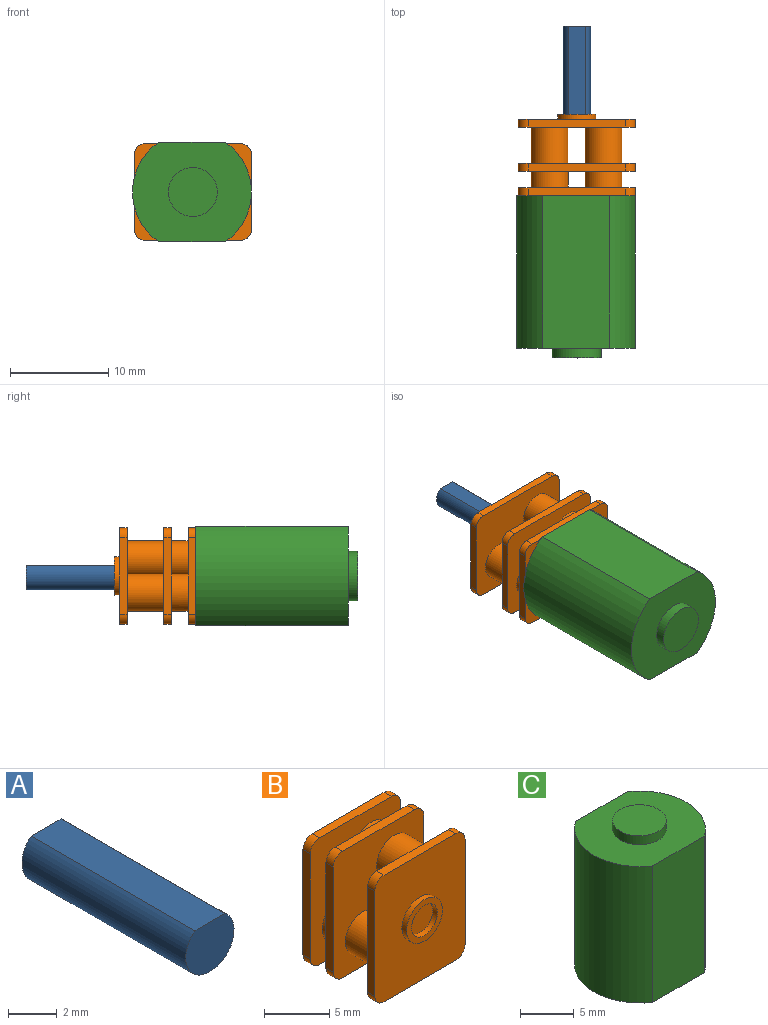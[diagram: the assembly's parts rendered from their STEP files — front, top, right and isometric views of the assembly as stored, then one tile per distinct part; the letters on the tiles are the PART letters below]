
ASSEMBLY  parts=3 mates=3
PART A: 4 faces, bbox 2.8x9.5x2.5 mm
  f0: cylinder r=1.4mm len=9.5mm, axis (0,1,0), area 65.8mm2, adj f1,f2,f3
  f1: plane 9.5x1.73mm, normal (0,0,1), area 16.5mm2, adj f0,f2,f3
  f2: plane 2.8x2.5mm, normal (0,-1,0), area 5.8mm2, adj f0,f1
  f3: plane 2.8x2.5mm, normal (0,1,0), area 5.8mm2, adj f0,f1
PART B: 38 faces, bbox 9.8x8.3x11.9 mm
  f0: plane 9.9x0.8mm, normal (1,0,0), area 7.9mm2, adj f19,f20,f26,f30
  f1: plane 9.9x0.8mm, normal (1,0,0), area 7.9mm2, adj f16,f17,f25,f28
  f2: plane 9.9x0.8mm, normal (-1,0,0), area 7.9mm2, adj f19,f20,f27,f33
  f3: plane 9.9x0.8mm, normal (-1,0,0), area 7.9mm2, adj f16,f17,f23,f29
  f4: plane 7.8x0.8mm, normal (0,0,-1), area 6.2mm2, adj f19,f20,f30,f33
  f5: plane 7.8x0.8mm, normal (0,0,-1), area 6.2mm2, adj f16,f17,f23,f25
  f6: plane 7.8x0.8mm, normal (0,0,-1), area 6.2mm2, adj f11,f15,f22,f24
  f7: cylinder r=1.9mm len=3.8mm, axis (0,1,0), area 44.2mm2, adj f16,f19
  f8: cylinder r=1.9mm len=3.8mm, axis (0,1,0), area 44.2mm2, adj f16,f19
  f9: cylinder r=1.9mm len=3.8mm, axis (0,1,0), area 20.3mm2, adj f11,f17
  f10: cylinder r=1.9mm len=3.8mm, axis (0,1,0), area 20.3mm2, adj f11,f17
  f11: plane 11.9x9.8mm, normal (0,-1,0), area 93.1mm2, adj f6,f9,f10,f12,f13,f14,f22,f24
  f12: plane 9.9x0.8mm, normal (1,0,0), area 7.9mm2, adj f11,f15,f24,f31
  f13: plane 7.8x0.8mm, normal (0,0,1), area 6.2mm2, adj f11,f15,f31,f32
  f14: plane 9.9x0.8mm, normal (-1,0,0), area 7.9mm2, adj f11,f15,f22,f32
  f15: plane 11.9x9.8mm, normal (0,1,0), area 115.8mm2, adj f6,f12,f13,f14,f22,f24,f31,f32
  f16: plane 11.9x9.8mm, normal (0,-1,0), area 93.1mm2, adj f1,f3,f5,f7,f8,f18,f23,f25
  f17: plane 11.9x9.8mm, normal (0,1,0), area 93.1mm2, adj f1,f3,f5,f9,f10,f18,f23,f25
  f18: plane 7.8x0.8mm, normal (0,0,1), area 6.2mm2, adj f16,f17,f28,f29
  f19: plane 11.9x9.8mm, normal (0,1,0), area 93.1mm2, adj f0,f2,f4,f7,f8,f21,f26,f27
  f20: plane 11.9x9.8mm, normal (0,-1,0), area 103.8mm2, adj f0,f2,f4,f21,f26,f27,f30,f33
  f21: plane 7.8x0.8mm, normal (0,0,1), area 6.2mm2, adj f19,f20,f26,f27
  f22: cylinder r=1mm len=1mm, axis (0,-1,0), area 1.3mm2, adj f6,f11,f14,f15
  f23: cylinder r=1mm len=1mm, axis (0,-1,0), area 1.3mm2, adj f3,f5,f16,f17
  f24: cylinder r=1mm len=1mm, axis (0,1,0), area 1.3mm2, adj f6,f11,f12,f15
  f25: cylinder r=1mm len=1mm, axis (0,1,0), area 1.3mm2, adj f1,f5,f16,f17
  f26: cylinder r=1mm len=1mm, axis (0,1,0), area 1.3mm2, adj f0,f19,f20,f21
  f27: cylinder r=1mm len=1mm, axis (0,-1,0), area 1.3mm2, adj f2,f19,f20,f21
  f28: cylinder r=1mm len=1mm, axis (0,1,0), area 1.3mm2, adj f1,f16,f17,f18
  f29: cylinder r=1mm len=1mm, axis (0,-1,0), area 1.3mm2, adj f3,f16,f17,f18
  f30: cylinder r=1mm len=1mm, axis (0,1,0), area 1.3mm2, adj f0,f4,f19,f20
  f31: cylinder r=1mm len=1mm, axis (0,-1,0), area 1.3mm2, adj f11,f12,f13,f15
  f32: cylinder r=1mm len=1mm, axis (0,1,0), area 1.3mm2, adj f11,f13,f14,f15
  f33: cylinder r=1mm len=1mm, axis (0,-1,0), area 1.3mm2, adj f2,f4,f19,f20
  f34: cylinder r=1.4mm len=2.8mm, axis (0,1,0), area 4.4mm2, adj f36,f37
  f35: cylinder r=1.95mm len=3.9mm, axis (0,1,0), area 6.1mm2, adj f20,f36
  f36: plane 3.9x3.9mm, normal (0,-1,0), area 5.8mm2, adj f34,f35
  f37: plane 2.8x2.8mm, normal (0,-1,0), area 6.2mm2, adj f34
PART C: 8 faces, bbox 12.1x10.1x16.5 mm
  f0: plane 15.5x6.8mm, normal (0,-1,0), area 105.4mm2, adj f1,f3,f4,f5
  f1: cylinder r=6.14mm len=15.5mm, axis (0,0,-1), area 183.9mm2, adj f0,f2,f4,f5
  f2: plane 15.5x6.8mm, normal (0,1,0), area 105.4mm2, adj f1,f3,f4,f5
  f3: cylinder r=6.14mm len=15.5mm, axis (0,0,-1), area 183.9mm2, adj f0,f2,f4,f5
  f4: plane 12.1x10.1mm, normal (0,0,1), area 86.6mm2, adj f0,f1,f2,f3,f6
  f5: plane 12.1x10.1mm, normal (0,0,-1), area 106.3mm2, adj f0,f1,f2,f3
  f6: cylinder r=2.5mm len=5mm, axis (0,0,-1), area 15.7mm2, adj f4,f7
  f7: plane 5x5mm, normal (0,0,1), area 19.6mm2, adj f6
PLACE A t=(-8.43,-6.86,-10.29)mm
PLACE B rot(axis=(0.71,0,0.71),180deg) t=(-8.43,-24.16,-10.29)mm
PLACE C rot(axis=(0,-0.71,0.71),180deg) t=(-8.51,-24.16,-10.29)mm
MATE planar B.f34 <-> C.f1  axis (0,-1,0) through (-8.43,-24.16,-10.29)mm
MATE revolute A.f0 <-> B.f34  axis (0,-1,0) through (-8.43,-16.36,-10.29)mm
MATE planar B.f34 <-> A.f0  axis (0,1,0) through (-8.43,-16.36,-10.29)mm
